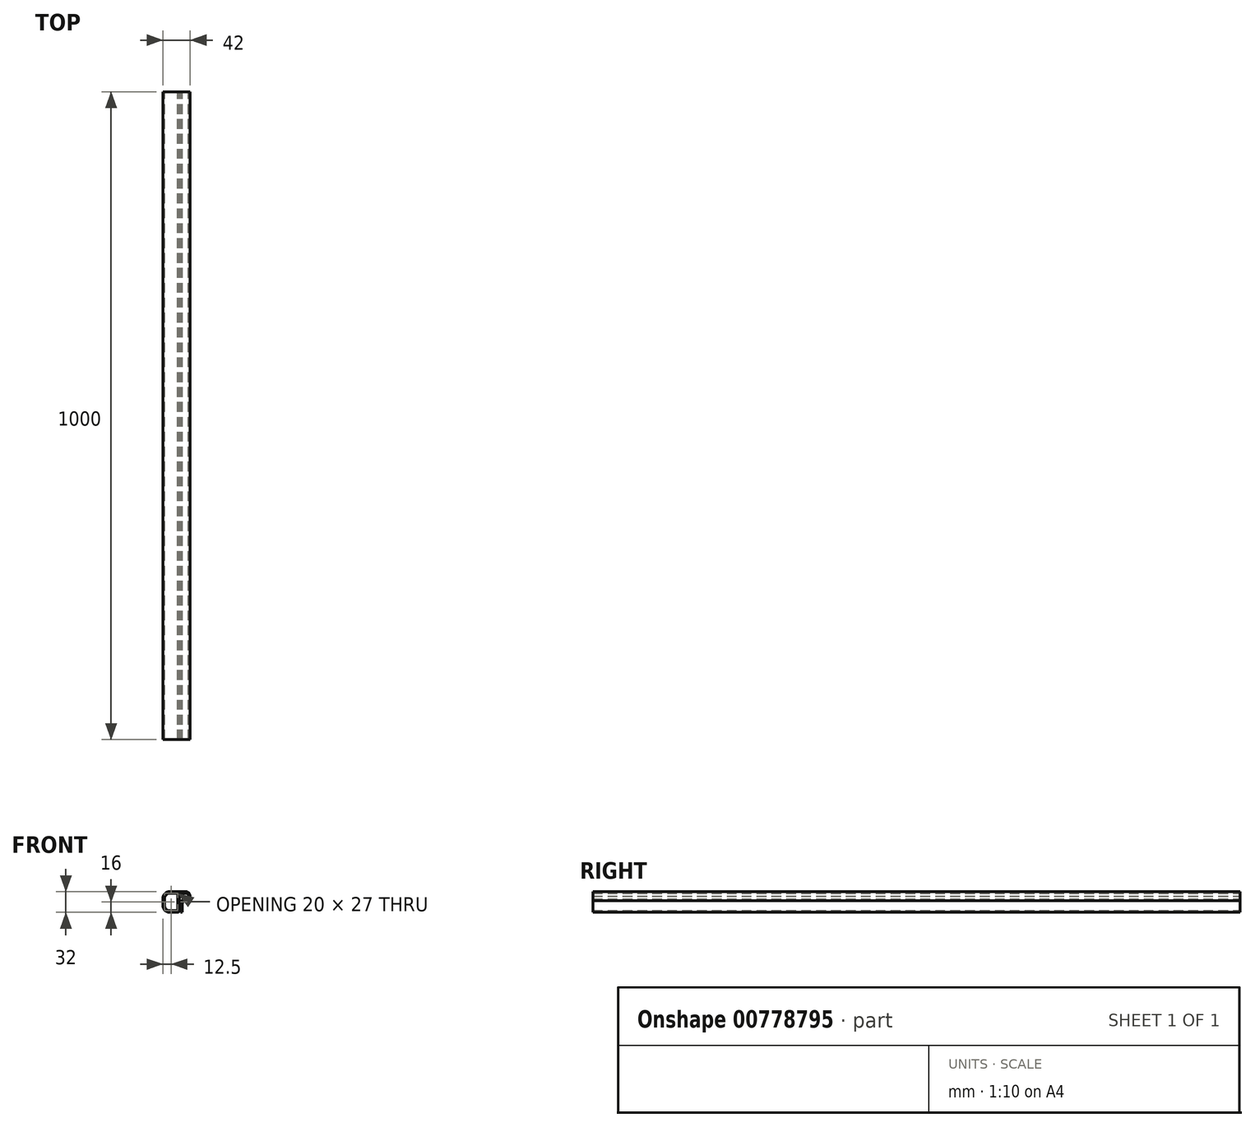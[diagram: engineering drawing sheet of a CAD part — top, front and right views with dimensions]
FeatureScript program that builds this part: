
annotation { "Feature Type Name" : "Feature", "Feature Type Description" : "" }
export const myFeature = defineFeature(function(context is Context, id is Id, definition is map)
    precondition{}
    {
        {
            var Q0;
            Q0=qCreatedBy(makeId("Front.planeOp"),FACE);
            var sketch = newSketch(context, id + "F0", { "sketchPlane" : qUnion([Q0])});
            skLineSegment(sketch, "E0", {"start": v(-2, 0) * mm, "end": v(-15, 0) * mm});
            skLineSegment(sketch, "E1", {"start": v(-25, 10) * mm, "end": v(-25, 22) * mm});
            skLineSegment(sketch, "E2", {"start": v(-15, 32) * mm, "end": v(10, 32) * mm});
            skLineSegment(sketch, "E3", {"start": v(17, 25) * mm, "end": v(17, 25) * mm});
            skLineSegment(sketch, "E4", {"start": v(10, 18) * mm, "end": v(10, 18) * mm});
            skLineSegment(sketch, "E5", {"start": v(5, 13) * mm, "end": v(5, 0) * mm});
            skLineSegment(sketch, "E6", {"start": v(0, 2) * mm, "end": v(0, 27.5) * mm});
            skLineSegment(sketch, "E7.0", {"start": v(-22.5, 10.5) * mm, "end": v(-22.5, 21.5) * mm});
            skLineSegment(sketch, "E7.1", {"start": v(-4.5, 2.5) * mm, "end": v(-14.5, 2.5) * mm});
            skLineSegment(sketch, "E7.2", {"start": v(-2.5, 4.5) * mm, "end": v(-2.5, 27.5) * mm});
            skLineSegment(sketch, "E8.0", {"start": v(2.5, 13.5) * mm, "end": v(2.5, 0) * mm});
            skLineSegment(sketch, "E8.1", {"start": v(9.5, 20.5) * mm, "end": v(9.5, 20.5) * mm});
            skLineSegment(sketch, "E8.2", {"start": v(14.5, 25.5) * mm, "end": v(14.5, 24.5) * mm});
            skLineSegment(sketch, "E8.3", {"start": v(-14.5, 29.5) * mm, "end": v(-4.5, 29.5) * mm});
            skLineSegment(sketch, "E9", {"start": v(2.5, 0) * mm, "end": v(5, 0) * mm});
            skLineSegment(sketch, "E10.trimOffspring", {"start": v(2, 29.5) * mm, "end": v(9.5, 29.5) * mm});
            skPoint(sketch, "E11.visualSharp", {"position": v(-25, 32) * mm});
            skArc(sketch, "E11.filletArc", {"start": v(-15, 32) * mm, "mid": v(-22.07, 29.07) * mm, "end": v(-25, 22) * mm});
            skPoint(sketch, "E12.visualSharp", {"position": v(17, 32) * mm});
            skArc(sketch, "E12.filletArc", {"start": v(17, 25) * mm, "mid": v(14.95, 29.95) * mm, "end": v(10, 32) * mm});
            skPoint(sketch, "E13.visualSharp", {"position": v(17, 18) * mm});
            skArc(sketch, "E13.filletArc", {"start": v(10, 18) * mm, "mid": v(14.95, 20.05) * mm, "end": v(17, 25) * mm});
            skPoint(sketch, "E14.visualSharp", {"position": v(5, 18) * mm});
            skArc(sketch, "E14.filletArc", {"start": v(10, 18) * mm, "mid": v(6.46, 16.54) * mm, "end": v(5, 13) * mm});
            skPoint(sketch, "E15.visualSharp", {"position": v(-25, 0) * mm});
            skArc(sketch, "E15.filletArc", {"start": v(-25, 10) * mm, "mid": v(-22.07, 2.93) * mm, "end": v(-15, 0) * mm});
            skPoint(sketch, "E16.visualSharp", {"position": v(0, 0) * mm});
            skArc(sketch, "E16.filletArc", {"start": v(-2, 0) * mm, "mid": v(-0.59, 0.59) * mm, "end": v(0, 2) * mm});
            skPoint(sketch, "E17.visualSharp", {"position": v(0, 29.5) * mm});
            skArc(sketch, "E17.filletArc", {"start": v(2, 29.5) * mm, "mid": v(0.59, 28.91) * mm, "end": v(0, 27.5) * mm});
            skPoint(sketch, "E18.visualSharp", {"position": v(-2.5, 29.5) * mm});
            skArc(sketch, "E18.filletArc", {"start": v(-2.5, 27.5) * mm, "mid": v(-3.09, 28.91) * mm, "end": v(-4.5, 29.5) * mm});
            skPoint(sketch, "E19.visualSharp", {"position": v(-22.5, 29.5) * mm});
            skArc(sketch, "E19.filletArc", {"start": v(-14.5, 29.5) * mm, "mid": v(-20.16, 27.16) * mm, "end": v(-22.5, 21.5) * mm});
            skPoint(sketch, "E20.visualSharp", {"position": v(-22.5, 2.5) * mm});
            skArc(sketch, "E20.filletArc", {"start": v(-22.5, 10.5) * mm, "mid": v(-20.16, 4.84) * mm, "end": v(-14.5, 2.5) * mm});
            skPoint(sketch, "E21.visualSharp", {"position": v(-2.5, 2.5) * mm});
            skArc(sketch, "E21.filletArc", {"start": v(-4.5, 2.5) * mm, "mid": v(-3.09, 3.09) * mm, "end": v(-2.5, 4.5) * mm});
            skPoint(sketch, "E22.visualSharp", {"position": v(2.5, 20.5) * mm});
            skArc(sketch, "E22.filletArc", {"start": v(9.5, 20.5) * mm, "mid": v(4.55, 18.45) * mm, "end": v(2.5, 13.5) * mm});
            skPoint(sketch, "E23.visualSharp", {"position": v(14.5, 29.5) * mm});
            skArc(sketch, "E23.filletArc", {"start": v(14.5, 24.5) * mm, "mid": v(13.04, 28.04) * mm, "end": v(9.5, 29.5) * mm});
            skPoint(sketch, "E24.visualSharp", {"position": v(14.5, 20.5) * mm});
            skArc(sketch, "E24.filletArc", {"start": v(9.5, 20.5) * mm, "mid": v(13.04, 21.96) * mm, "end": v(14.5, 25.5) * mm});
            skSolve(sketch);
        }
        {
            var Q0;
            Q0=qSketchRegion(id+"F0",true);
            extrude(context, id + "F1", {"entities" : qUnion([Q0]), "depth" : 1000 * mm, "offsetDistance" : 25 * mm});
        }
    });
